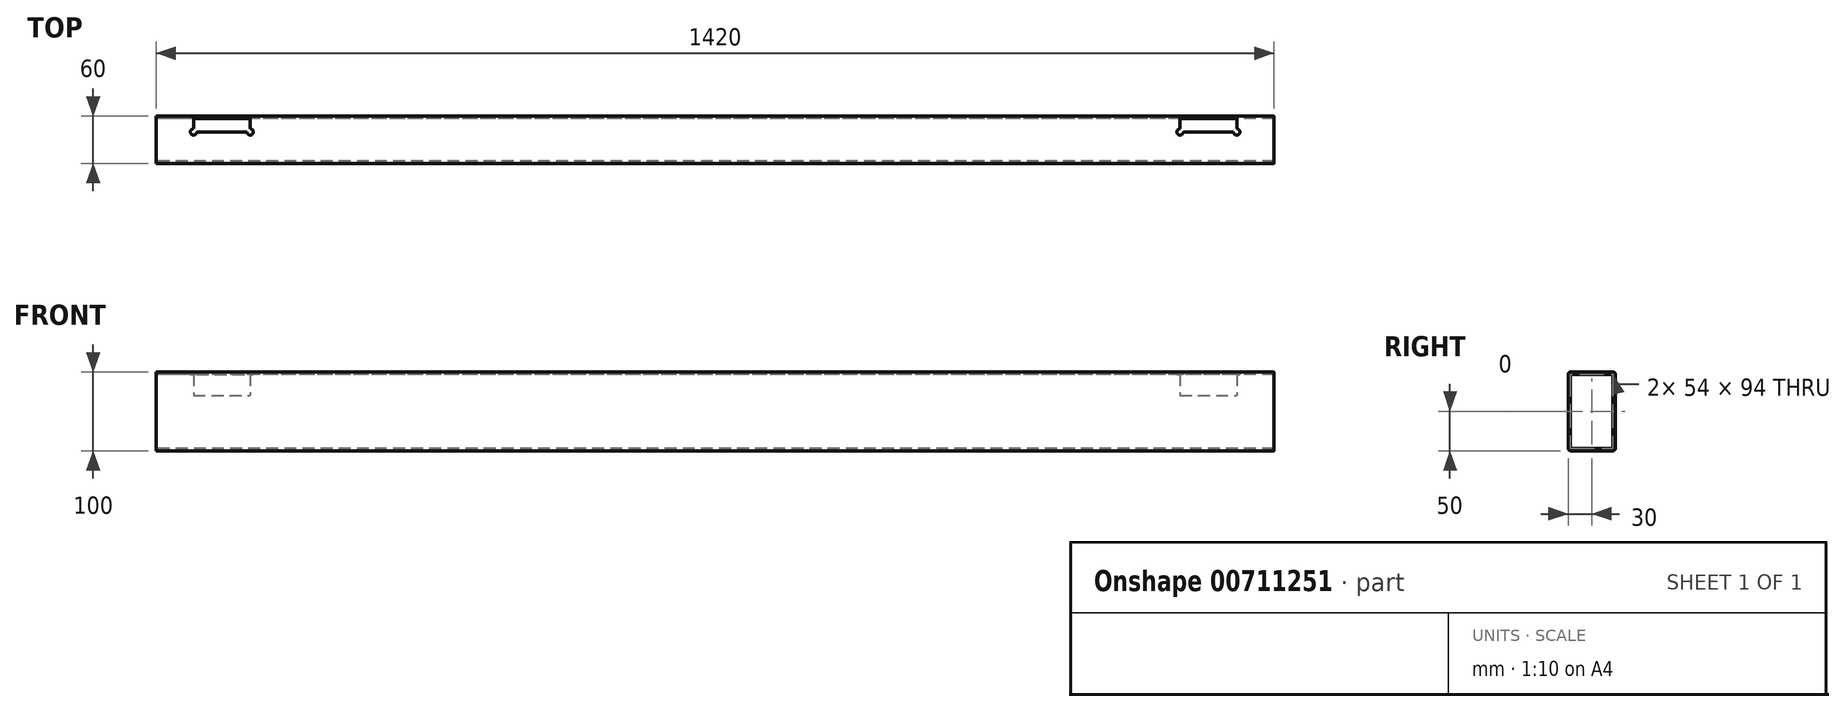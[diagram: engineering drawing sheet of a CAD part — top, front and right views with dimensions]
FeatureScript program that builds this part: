
annotation { "Feature Type Name" : "Feature", "Feature Type Description" : "" }
export const myFeature = defineFeature(function(context is Context, id is Id, definition is map)
    precondition{}
    {
        {
            var Q0;
            Q0=qCreatedBy(makeId("Right.planeOp"),FACE);
            var sketch = newSketch(context, id + "F0", { "sketchPlane" : qUnion([Q0])});
            skLineSegment(sketch, "E0.bottom", {"start": v(27, 50) * mm, "end": v(-27, 50) * mm});
            skLineSegment(sketch, "E0.top", {"start": v(27, -50) * mm, "end": v(-27, -50) * mm});
            skLineSegment(sketch, "E0.left", {"start": v(30, 47) * mm, "end": v(30, -47) * mm});
            skLineSegment(sketch, "E0.right", {"start": v(-30, 47) * mm, "end": v(-30, -47) * mm});
            skPoint(sketch, "E0.middle", {"position": v(0, 0) * mm});
            skPoint(sketch, "E1.visualSharp", {"position": v(-30, 50) * mm});
            skArc(sketch, "E1.filletArc", {"start": v(-27, 50) * mm, "mid": v(-29.12, 49.12) * mm, "end": v(-30, 47) * mm});
            skPoint(sketch, "E2.visualSharp", {"position": v(30, 50) * mm});
            skArc(sketch, "E2.filletArc", {"start": v(30, 47) * mm, "mid": v(29.12, 49.12) * mm, "end": v(27, 50) * mm});
            skPoint(sketch, "E3.visualSharp", {"position": v(30, -50) * mm});
            skArc(sketch, "E3.filletArc", {"start": v(27, -50) * mm, "mid": v(29.12, -49.12) * mm, "end": v(30, -47) * mm});
            skPoint(sketch, "E4.visualSharp", {"position": v(-30, -50) * mm});
            skArc(sketch, "E4.filletArc", {"start": v(-30, -47) * mm, "mid": v(-29.12, -49.12) * mm, "end": v(-27, -50) * mm});
            skLineSegment(sketch, "E5.bottom", {"start": v(27, 47) * mm, "end": v(-27, 47) * mm});
            skLineSegment(sketch, "E5.top", {"start": v(27, -47) * mm, "end": v(-27, -47) * mm});
            skLineSegment(sketch, "E5.left", {"start": v(27, 47) * mm, "end": v(27, -47) * mm});
            skLineSegment(sketch, "E5.right", {"start": v(-27, 47) * mm, "end": v(-27, -47) * mm});
            skSolve(sketch);
        }
        {
            var Q0;
            Q0=makeQuery(id+"F0.imprint","IMPRINT",FACE,{"disambiguationData":[TD([[makeQuery(id+"F0.imprint","IMPRINT",EDGE,{"derivedFrom":sQuery(id+"F0.wireOp",EDGE,"E0.bottom")}),1.0]])]});
            extrude(context, id + "F1", {"entities" : qUnion([Q0]), "endBound" : BoundingType.SYMMETRIC, "depth" : 1420 * mm, "offsetDistance" : 25 * mm});
        }
        {
            var Q0;
            Q0=qCreatedBy(makeId("Top.planeOp"),FACE);
            var sketch = newSketch(context, id + "F2", { "sketchPlane" : qUnion([Q0])});
            skLineSegment(sketch, "E6.bottom", {"start": v(-690, 50) * mm, "end": v(-672.6, 50) * mm});
            skLineSegment(sketch, "E6.top", {"start": v(-710, -30) * mm, "end": v(710, -30) * mm});
            skLineSegment(sketch, "E6.left", {"start": v(-710, 30) * mm, "end": v(-710, -30) * mm});
            skLineSegment(sketch, "E6.right", {"start": v(710, 30) * mm, "end": v(710, -30) * mm});
            skPoint(sketch, "E6.middle", {"position": v(0, 10) * mm});
            skLineSegment(sketch, "E7.0", {"start": v(-560, 50) * mm, "end": v(-560, 44) * mm});
            skLineSegment(sketch, "E8.0", {"start": v(-500, 50) * mm, "end": v(-500, 44) * mm});
            skLineSegment(sketch, "E9.0", {"start": v(-556, 40) * mm, "end": v(-504, 40) * mm});
            skLineSegment(sketch, "E10.0", {"start": v(560, 50) * mm, "end": v(560, 44) * mm});
            skLineSegment(sketch, "E11.0", {"start": v(500, 50) * mm, "end": v(500, 44) * mm});
            skLineSegment(sketch, "E12.trimOffspring", {"start": v(504, 40) * mm, "end": v(556, 40) * mm});
            skLineSegment(sketch, "E13.trimOffspring", {"start": v(-500, 50) * mm, "end": v(500, 50) * mm});
            skLineSegment(sketch, "E14.trimOffspring", {"start": v(560, 50) * mm, "end": v(580.6, 50) * mm});
            skPoint(sketch, "E15.visualSharp", {"position": v(-710, 50) * mm});
            skArc(sketch, "E15.filletArc", {"start": v(-690, 50) * mm, "mid": v(-704.14, 44.14) * mm, "end": v(-710, 30) * mm});
            skArc(sketch, "E16", {"start": v(-560, 44) * mm, "mid": v(-562.83, 37.17) * mm, "end": v(-556, 40) * mm});
            skArc(sketch, "E17", {"start": v(-504, 40) * mm, "mid": v(-497.17, 37.17) * mm, "end": v(-500, 44) * mm});
            skArc(sketch, "E18", {"start": v(556, 40) * mm, "mid": v(562.83, 37.17) * mm, "end": v(560, 44) * mm});
            skArc(sketch, "E19", {"start": v(500, 44) * mm, "mid": v(497.17, 37.17) * mm, "end": v(504, 40) * mm});
            skPoint(sketch, "E20.visualSharp", {"position": v(710, 50) * mm});
            skArc(sketch, "E20.filletArc", {"start": v(710, 30) * mm, "mid": v(704.14, 44.14) * mm, "end": v(690, 50) * mm});
            skLineSegment(sketch, "E21.0", {"start": v(-662.6, 40) * mm, "end": v(-662.6, 14) * mm});
            skLineSegment(sketch, "E22.0", {"start": v(-590.6, 40) * mm, "end": v(-590.6, 14) * mm});
            skLineSegment(sketch, "E23.0", {"start": v(-658.6, 10) * mm, "end": v(-594.6, 10) * mm});
            skArc(sketch, "E24", {"start": v(-662.6, 14) * mm, "mid": v(-665.44, 7.17) * mm, "end": v(-658.6, 10) * mm});
            skArc(sketch, "E25", {"start": v(-594.6, 10) * mm, "mid": v(-587.78, 7.17) * mm, "end": v(-590.6, 14) * mm});
            skLineSegment(sketch, "E26.trimOffspring", {"start": v(-580.6, 50) * mm, "end": v(-560, 50) * mm});
            skLineSegment(sketch, "E27.MirrorCS", {"start": v(662.6, 40) * mm, "end": v(662.6, 14) * mm});
            skLineSegment(sketch, "E28.MirrorCS", {"start": v(590.6, 40) * mm, "end": v(590.6, 14) * mm});
            skLineSegment(sketch, "E29.MirrorCS", {"start": v(658.6, 10) * mm, "end": v(594.6, 10) * mm});
            skArc(sketch, "E30.MirrorCS", {"start": v(594.6, 10) * mm, "mid": v(587.78, 7.17) * mm, "end": v(590.6, 14) * mm});
            skArc(sketch, "E31.MirrorCS", {"start": v(662.6, 14) * mm, "mid": v(665.44, 7.17) * mm, "end": v(658.6, 10) * mm});
            skLineSegment(sketch, "E32.trimOffspring", {"start": v(672.6, 50) * mm, "end": v(690, 50) * mm});
            skPoint(sketch, "E33.visualSharp", {"position": v(590.6, 50) * mm});
            skArc(sketch, "E33.filletArc", {"start": v(590.6, 40) * mm, "mid": v(587.68, 47.07) * mm, "end": v(580.6, 50) * mm});
            skPoint(sketch, "E34.visualSharp", {"position": v(662.6, 50) * mm});
            skArc(sketch, "E34.filletArc", {"start": v(672.6, 50) * mm, "mid": v(665.54, 47.07) * mm, "end": v(662.6, 40) * mm});
            skPoint(sketch, "E35.visualSharp", {"position": v(-662.6, 50) * mm});
            skArc(sketch, "E35.filletArc", {"start": v(-662.6, 40) * mm, "mid": v(-665.54, 47.07) * mm, "end": v(-672.6, 50) * mm});
            skPoint(sketch, "E36.visualSharp", {"position": v(-590.6, 50) * mm});
            skArc(sketch, "E36.filletArc", {"start": v(-580.6, 50) * mm, "mid": v(-587.68, 47.07) * mm, "end": v(-590.6, 40) * mm});
            skLineSegment(sketch, "E37", {"start": v(-662.6, 40) * mm, "end": v(-590.6, 40) * mm});
            skLineSegment(sketch, "E38", {"start": v(590.6, 40) * mm, "end": v(662.6, 40) * mm});
            skSolve(sketch);
        }
        {
            var Q0;
            Q0=makeQuery(id+"F2.imprint","IMPRINT",FACE,{"disambiguationData":[TD([[makeQuery(id+"F2.imprint","IMPRINT",EDGE,{"derivedFrom":sQuery(id+"F2.wireOp",EDGE,"E21.0")}),1.0]])]});
            extrude(context, id + "F3", {"entities" : qUnion([Q0]), "operationType" : NewBodyOperationType.REMOVE, "depth" : 55 * mm, "offsetDistance" : 25 * mm, "hasSecondDirection" : true, "secondDirectionOppositeDirection" : true, "secondDirectionDepth" : -20 * mm});
        }
        {
            var Q0;
            Q0=makeQuery(id+"F2.imprint","IMPRINT",FACE,{"disambiguationData":[TD([[makeQuery(id+"F2.imprint","IMPRINT",EDGE,{"derivedFrom":sQuery(id+"F2.wireOp",EDGE,"E27.MirrorCS")}),-1.0]])]});
            extrude(context, id + "F4", {"entities" : qUnion([Q0]), "operationType" : NewBodyOperationType.REMOVE, "depth" : 55 * mm, "offsetDistance" : 25 * mm, "hasSecondDirection" : true, "secondDirectionOppositeDirection" : true, "secondDirectionDepth" : -20 * mm});
        }
    });
